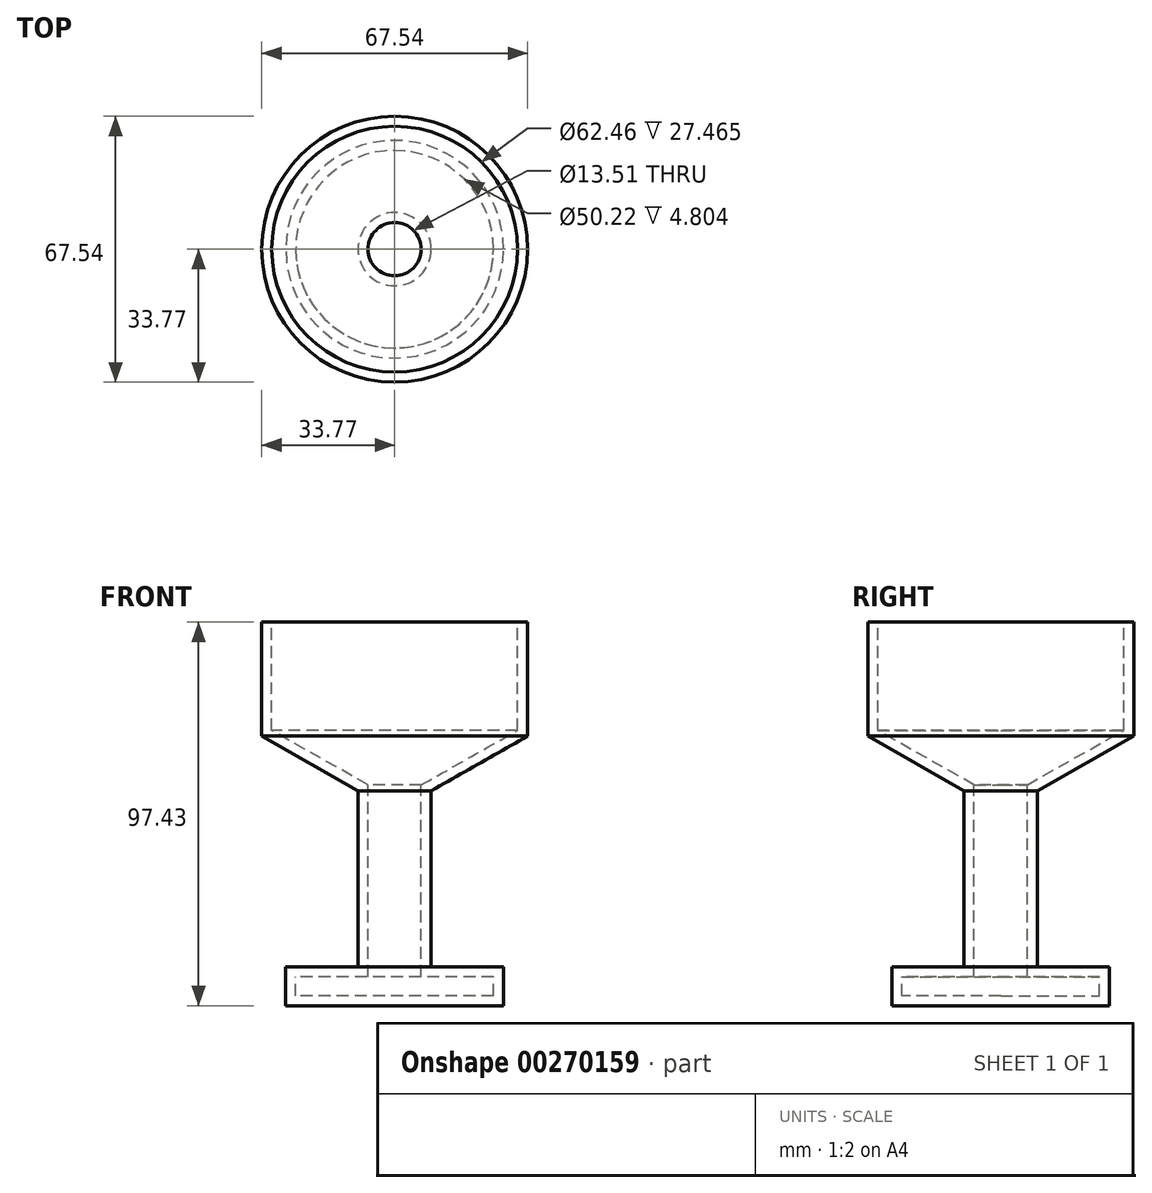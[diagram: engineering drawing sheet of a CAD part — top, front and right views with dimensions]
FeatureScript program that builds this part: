
annotation { "Feature Type Name" : "Feature", "Feature Type Description" : "" }
export const myFeature = defineFeature(function(context is Context, id is Id, definition is map)
    precondition{}
    {
        {
            var Q0;
            Q0=qCreatedBy(makeId("Front.planeOp"),FACE);
            var sketch = newSketch(context, id + "F0", { "sketchPlane" : qUnion([Q0])});
            skLineSegment(sketch, "E0", {"start": v(0, 56.48) * mm, "end": v(-33.77, 56.48) * mm});
            skLineSegment(sketch, "E1", {"start": v(-33.77, 56.48) * mm, "end": v(-33.77, 27.53) * mm});
            skLineSegment(sketch, "E2", {"start": v(-33.77, 27.53) * mm, "end": v(-9.3, 13.65) * mm});
            skLineSegment(sketch, "E3", {"start": v(-9.3, 13.65) * mm, "end": v(-9.3, -31.06) * mm});
            skLineSegment(sketch, "E4", {"start": v(-9.3, -31.06) * mm, "end": v(-27.65, -31.06) * mm});
            skLineSegment(sketch, "E5", {"start": v(-27.65, -31.06) * mm, "end": v(-27.65, -40.95) * mm});
            skLineSegment(sketch, "E6", {"start": v(-27.65, -40.95) * mm, "end": v(0, -40.95) * mm});
            skLineSegment(sketch, "E7", {"start": v(0, 56.48) * mm, "end": v(0, -40.95) * mm});
            skSolve(sketch);
        }
        {
            var Q0;
            Q0 = qSketchRegion(id + "F0", true);
            var Q1;
            Q1=sQuery(id+"F0.wireOp",EDGE,"E7");
            revolve(context, id + "F1", {"entities" : qUnion([Q0]), "axis" : qUnion([Q1]), "revolveType" : RevolveType.FULL});
        }
        {
            var Q0;
            Q0=makeQuery(id+"F1.opRevolve","SWEPT_FACE",FACE,{"disambiguationData":[OSD([sQuery(id+"F0.wireOp",EDGE,"E0")])]});
            shell(context, id + "F2", {"entities" : qUnion([Q0]), "thickness" : 2.54 * mm});
        }
    });
